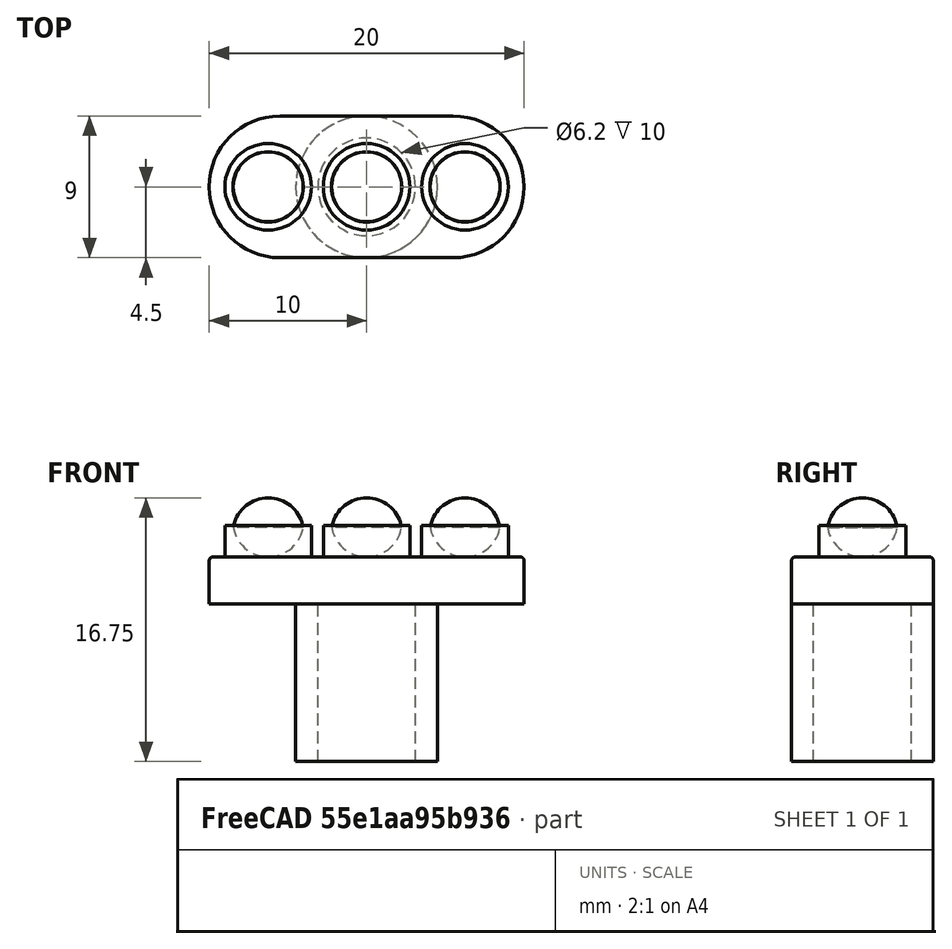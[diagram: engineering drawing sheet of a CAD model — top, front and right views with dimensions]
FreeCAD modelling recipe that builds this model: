
FCSTD DOCUMENT  (FreeCAD 0.17R13541 (Git))
Label: Landing light knob
License: All rights reserved
LicenseURL: http://en.wikipedia.org/wiki/All_rights_reserved
objects: Part::Cylinder×7, Part::Sphere×6, Part::Cut×4, Part::MultiFuse×4, Part::Feature×3, Part::Box×1, Part::Fillet×1
note: 26 computed .brp shape members not serialized (recipe doc carries the construction recipe); baked Part::Feature solids carry a one-line shape summary decoded from their .brp

FEATURE [Part::Cylinder] Cylinder  label="Cilindro base"
  Angle = 360
  AttacherType = Attacher::AttachEngine3D
  Height = 10
  Radius = 4.5
FEATURE [Part::Cylinder] Cylinder001  label="Taladro 1"
  Angle = 360
  AttacherType = Attacher::AttachEngine3D
  Height = 10
  Radius = 3.1
FEATURE [Part::Cut] Cut  label="Cilindro base taladrado"
  Base = -> Cylinder
  Refine = true
  Tool = -> Cylinder001
FEATURE [Part::Box] Box  label="Base"
  AttacherType = Attacher::AttachEngine3D
  Height = 3
  Length = 11
  Placement = pos=(-5.5,-4.5,10) rot=(0,0,1;0rad)
  Width = 9
FEATURE [Part::Cylinder] Cylinder002  label="Cilindro chaflan 1"
  Angle = 180
  AttacherType = Attacher::AttachEngine3D
  Height = 3
  Placement = pos=(5.5,0,10) rot=(0,0,-1;1.5708rad)
  Radius = 4.5
FEATURE [Part::Cylinder] Cylinder003  label="Cilindro chaflan 2"
  Angle = 180
  AttacherType = Attacher::AttachEngine3D
  Height = 3
  Placement = pos=(-5.5,0,10) rot=(0,0,1;1.5708rad)
  Radius = 4.5
FEATURE [Part::MultiFuse] Fusion  label="Base redondeada"
  Refine = true
  Shapes = -> [Box,Cylinder002,Cylinder003]
FEATURE [Part::Cylinder] Cylinder004  label="Cilindro esfera 1"
  Angle = 360
  AttacherType = Attacher::AttachEngine3D
  Height = 2
  Placement = pos=(6.25,0,13) rot=(0,0,1;0rad)
  Radius = 2.75
FEATURE [Part::Cylinder] Cylinder005  label="Cilindro esfera 2"
  Angle = 360
  AttacherType = Attacher::AttachEngine3D
  Height = 2
  Placement = pos=(0,0,13) rot=(0,0,1;0rad)
  Radius = 2.75
FEATURE [Part::Cylinder] Cylinder006  label="Cilindro esfera 3"
  Angle = 360
  AttacherType = Attacher::AttachEngine3D
  Height = 2
  Placement = pos=(-6.25,0,13) rot=(0,0,1;0rad)
  Radius = 2.75
FEATURE [Part::Sphere] Sphere  label="Esfera 1"
  Angle1 = -90
  Angle2 = 90
  Angle3 = 360
  AttacherType = Attacher::AttachEngine3D
  Placement = pos=(6.25,0,14.5) rot=(0,0,1;0rad)
  Radius = 2.25
FEATURE [Part::Sphere] Sphere001  label="Esfera 2"
  Angle1 = -90
  Angle2 = 90
  Angle3 = 360
  AttacherType = Attacher::AttachEngine3D
  Placement = pos=(0,0,14.5) rot=(0,0,1;0rad)
  Radius = 2.25
FEATURE [Part::Sphere] Sphere002  label="Esfera 3"
  Angle1 = -90
  Angle2 = 90
  Angle3 = 360
  AttacherType = Attacher::AttachEngine3D
  Placement = pos=(-6.25,0,14.5) rot=(0,0,1;0rad)
  Radius = 2.25
FEATURE [Part::Sphere] Sphere003  label="Esfera 1 taladro"
  Angle1 = -90
  Angle2 = 90
  Angle3 = 360
  AttacherType = Attacher::AttachEngine3D
  Placement = pos=(6.25,0,15.25) rot=(0,0,1;0rad)
  Radius = 2.25
FEATURE [Part::Cut] Cut001  label="Cilindro esfera recortado 1"
  Base = -> Cylinder004
  Refine = true
  Tool = -> Sphere003
FEATURE [Part::Sphere] Sphere004  label="Esfera 1 taladro 2"
  Angle1 = -90
  Angle2 = 90
  Angle3 = 360
  AttacherType = Attacher::AttachEngine3D
  Placement = pos=(0,0,15.25) rot=(0,0,1;0rad)
  Radius = 2.25
FEATURE [Part::Sphere] Sphere005  label="Esfera 1 taladro 3"
  Angle1 = -90
  Angle2 = 90
  Angle3 = 360
  AttacherType = Attacher::AttachEngine3D
  Placement = pos=(-6.25,0,15.25) rot=(0,0,1;0rad)
  Radius = 2.25
FEATURE [Part::Cut] Cut002  label="Cilindro esfera recortado 2"
  Base = -> Cylinder005
  Refine = true
  Tool = -> Sphere004
FEATURE [Part::Cut] Cut003  label="Cilindro esfera recortado 3"
  Base = -> Cylinder006
  Refine = true
  Tool = -> Sphere005
FEATURE [Part::Feature] Cut001_solid  label="Cilindro esfera recortado 1 (Solid)"
  shape: bbox 5.5 x 5.5 x 2 mm, 4 faces (baked)
FEATURE [Part::Feature] Cut002_solid  label="Cilindro esfera recortado 2 (Solid)"
  shape: bbox 5.5 x 5.5 x 2 mm, 4 faces (baked)
FEATURE [Part::Feature] Cut003_solid  label="Cilindro esfera recortado 3 (Solid)"
  shape: bbox 5.5 x 5.5 x 2 mm, 4 faces (baked)
FEATURE [Part::MultiFuse] Fusion001  label="Base001"
  Refine = true
  Shapes = -> [Cut001_solid,Cut002_solid,Cut003_solid,Fusion]
FEATURE [Part::MultiFuse] Fusion002  label="Estructura"
  Refine = true
  Shapes = -> [Cut,Fusion001]
FEATURE [Part::MultiFuse] Fusion003  label="Estructura con esferas"
  Refine = true
  Shapes = -> [Sphere,Sphere001,Sphere002,Fusion002]
FEATURE [Part::Fillet] Fillet  label="Landing knob final"
  Base = -> Fusion003
  Edges = 3 edges r=0.25: [Edge19,Edge20,Edge21]
